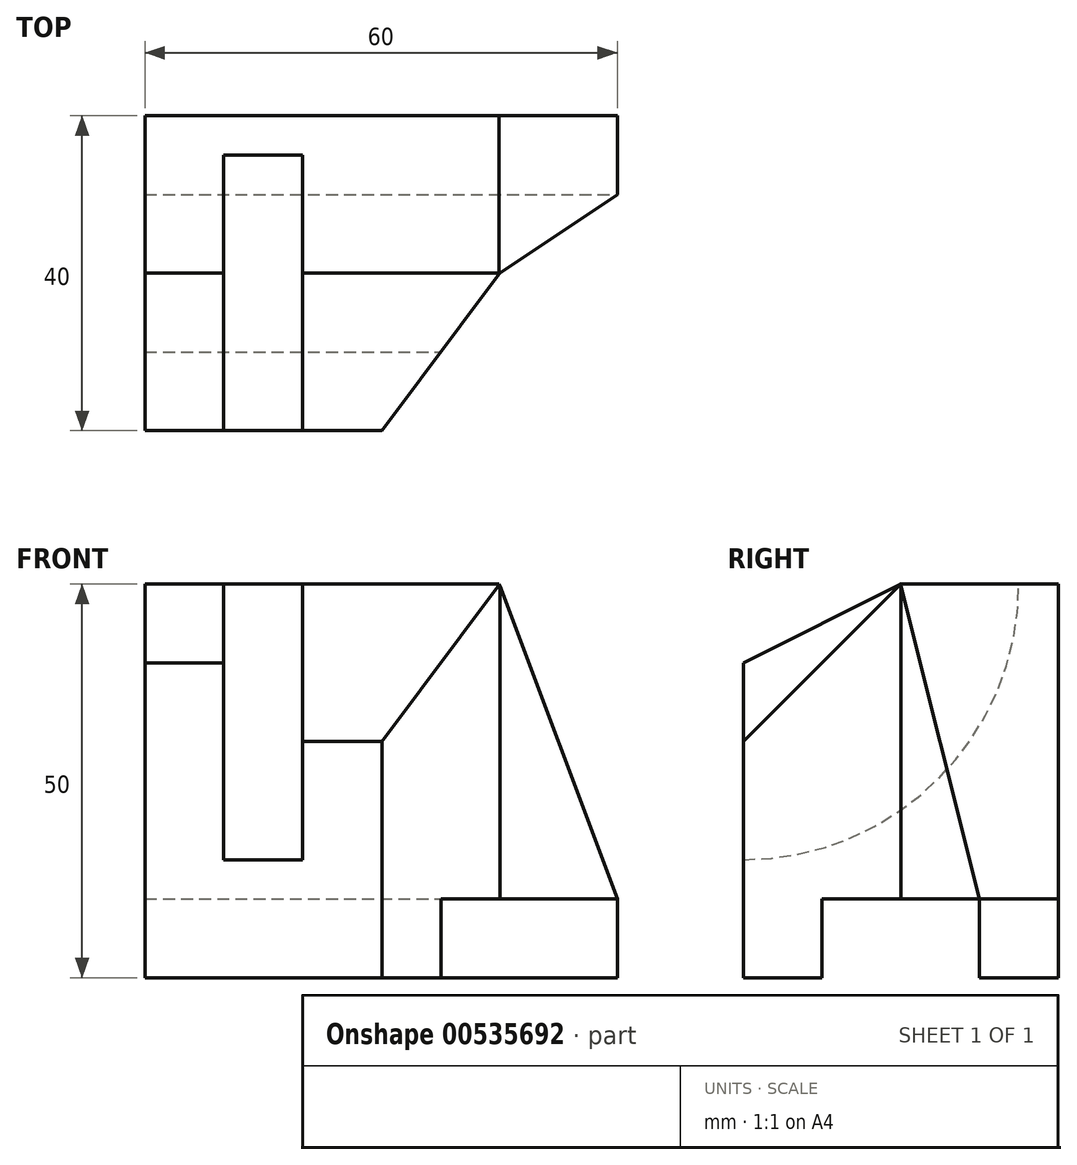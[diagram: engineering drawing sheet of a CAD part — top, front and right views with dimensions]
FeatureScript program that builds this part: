
annotation { "Feature Type Name" : "Feature", "Feature Type Description" : "" }
export const myFeature = defineFeature(function(context is Context, id is Id, definition is map)
    precondition{}
    {
        {
            var Q0;
            Q0=qCreatedBy(makeId("Top.planeOp"),FACE);
            var sketch = newSketch(context, id + "F0", { "sketchPlane" : qUnion([Q0])});
            skLineSegment(sketch, "E0.bottom", {"start": v(0, 0) * mm, "end": v(60, 0) * mm});
            skLineSegment(sketch, "E0.top", {"start": v(0, 40) * mm, "end": v(60, 40) * mm});
            skLineSegment(sketch, "E0.left", {"start": v(0, 0) * mm, "end": v(0, 40) * mm});
            skLineSegment(sketch, "E0.right", {"start": v(60, 0) * mm, "end": v(60, 40) * mm});
            skSolve(sketch);
        }
        {
            var Q0;
            Q0 = qSketchRegion(id + "F0", true);
            extrude(context, id + "F1", {"entities" : qUnion([Q0]), "depth" : 50 * mm, "offsetDistance" : 25 * mm});
        }
        {
            var Q0;
            Q0=makeQuery(id+"F1.opExtrude","SWEPT_FACE",FACE,{"disambiguationData":[OSD([sQuery(id+"F0.wireOp",EDGE,"E0.right")])]});
            var sketch = newSketch(context, id + "F2", { "sketchPlane" : qUnion([Q0])});
            skLineSegment(sketch, "E1", {"start": v(0, 0) * mm, "end": v(10, 0) * mm});
            skLineSegment(sketch, "E2.bottom", {"start": v(10, 0) * mm, "end": v(30, 0) * mm});
            skLineSegment(sketch, "E2.top", {"start": v(10, 10) * mm, "end": v(30, 10) * mm});
            skLineSegment(sketch, "E2.left", {"start": v(10, 0) * mm, "end": v(10, 10) * mm});
            skLineSegment(sketch, "E2.right", {"start": v(30, 0) * mm, "end": v(30, 10) * mm});
            skSolve(sketch);
        }
        {
            var Q0;
            Q0 = qSketchRegion(id + "F2", true);
            extrude(context, id + "F3", {"entities" : qUnion([Q0]), "operationType" : NewBodyOperationType.REMOVE, "endBound" : BoundingType.UP_TO_NEXT, "oppositeDirection" : true, "depth" : 25 * mm, "offsetDistance" : 25 * mm});
        }
        {
            var Q0;
            Q0=qCreatedBy(makeId("Right.planeOp"),FACE);
            cPlane(context, id + "F4", {"entities" : qUnion([Q0]), "cplaneType" : CPlaneType.OFFSET, "offset" : 10 * mm, "width" : 150 * mm, "height" : 150 * mm});
        }
        {
            var Q0;
            Q0=qCreatedBy(id+"F4.planeOp",FACE);
            cPlane(context, id + "F5", {"entities" : qUnion([Q0]), "cplaneType" : CPlaneType.OFFSET, "offset" : 10 * mm, "width" : 150 * mm, "height" : 150 * mm});
        }
        {
            var Q0;
            Q0=makeQuery(id+"F1.opExtrude","SWEPT_FACE",FACE,{"disambiguationData":[OSD([sQuery(id+"F0.wireOp",EDGE,"E0.left")])]});
            var sketch = newSketch(context, id + "F6", { "sketchPlane" : qUnion([Q0])});
            skLineSegment(sketch, "E3", {"start": v(0, 50) * mm, "end": v(0, 40) * mm});
            skLineSegment(sketch, "E4", {"start": v(0, 50) * mm, "end": v(-20, 50) * mm});
            skLineSegment(sketch, "E5", {"start": v(-20, 50) * mm, "end": v(0, 40) * mm});
            skSolve(sketch);
        }
        {
            var Q0;
            Q0 = qSketchRegion(id + "F6", true);
            var Q1;
            Q1=qCreatedBy(id+"F4.planeOp",FACE);
            extrude(context, id + "F7", {"entities" : qUnion([Q0]), "operationType" : NewBodyOperationType.REMOVE, "endBound" : BoundingType.UP_TO_SURFACE, "oppositeDirection" : true, "depth" : 25 * mm, "endBoundEntityFace" : qUnion([Q1]), "offsetDistance" : 25 * mm});
        }
        {
            var Q0;
            Q0=qCreatedBy(makeId("Right.planeOp"),FACE);
            cPlane(context, id + "F8", {"entities" : qUnion([Q0]), "cplaneType" : CPlaneType.OFFSET, "offset" : 45 * mm, "width" : 150 * mm, "height" : 150 * mm});
        }
        {
            var Q0;
            Q0=qCreatedBy(id+"F5.planeOp",FACE);
            var sketch = newSketch(context, id + "F9", { "sketchPlane" : qUnion([Q0])});
            skLineSegment(sketch, "E6", {"start": v(0, 50) * mm, "end": v(0, 30) * mm});
            skLineSegment(sketch, "E7", {"start": v(0, 50) * mm, "end": v(20, 50) * mm});
            skLineSegment(sketch, "E8", {"start": v(20, 50) * mm, "end": v(0, 30) * mm});
            skSolve(sketch);
        }
        {
            var Q0;
            Q0 = qSketchRegion(id + "F9", true);
            var Q1;
            Q1=qCreatedBy(id+"F8.planeOp",FACE);
            extrude(context, id + "F10", {"entities" : qUnion([Q0]), "operationType" : NewBodyOperationType.REMOVE, "endBound" : BoundingType.UP_TO_SURFACE, "depth" : 25 * mm, "endBoundEntityFace" : qUnion([Q1]), "offsetDistance" : 25 * mm});
        }
        {
            var Q0;
            Q0=qCreatedBy(id+"F4.planeOp",FACE);
            var sketch = newSketch(context, id + "F11", { "sketchPlane" : qUnion([Q0])});
            skCircle(sketch, "E9", {"center": v(0, 50) * mm, "radius": 35 * mm});
            skSolve(sketch);
        }
        {
            var Q0;
            Q0 = qSketchRegion(id + "F11", true);
            var Q1;
            Q1=qCreatedBy(id+"F5.planeOp",FACE);
            extrude(context, id + "F12", {"entities" : qUnion([Q0]), "operationType" : NewBodyOperationType.REMOVE, "endBound" : BoundingType.UP_TO_SURFACE, "depth" : 25 * mm, "endBoundEntityFace" : qUnion([Q1]), "offsetDistance" : 25 * mm});
        }
        {
            var Q0;
            Q0=qCreatedBy(makeId("Top.planeOp"),FACE);
            cPlane(context, id + "F13", {"entities" : qUnion([Q0]), "cplaneType" : CPlaneType.OFFSET, "offset" : 50 * mm, "width" : 150 * mm, "height" : 150 * mm});
        }
        {
            var Q0;
            Q0=qCreatedBy(id+"F13.planeOp",FACE);
            var sketch = newSketch(context, id + "F14", { "sketchPlane" : qUnion([Q0])});
            skLineSegment(sketch, "E10", {"start": v(45.1, 0) * mm, "end": v(45.1, 20) * mm});
            skLineSegment(sketch, "E11", {"start": v(45.1, 0) * mm, "end": v(30.1, 0) * mm});
            skLineSegment(sketch, "E12", {"start": v(45.1, 20) * mm, "end": v(30.1, 0) * mm});
            skSolve(sketch);
        }
        {
            var Q0;
            Q0 = qSketchRegion(id + "F14", true);
            extrude(context, id + "F15", {"entities" : qUnion([Q0]), "operationType" : NewBodyOperationType.REMOVE, "oppositeDirection" : true, "depth" : 50 * mm, "offsetDistance" : 25 * mm});
        }
        {
            var Q0;
            Q0=makeQuery(id+"F1.opExtrude","CAP_FACE",FACE,{"disambiguationData":[OSD([sQuery(id+"F0.wireOp",EDGE,"E0.bottom"),sQuery(id+"F0.wireOp",EDGE,"E0.top"),sQuery(id+"F0.wireOp",EDGE,"E0.left"),sQuery(id+"F0.wireOp",EDGE,"E0.right")])],"isStart":false});
            var sketch = newSketch(context, id + "F16", { "sketchPlane" : qUnion([Q0])});
            skLineSegment(sketch, "E13", {"start": v(60, 40) * mm, "end": v(60, 30) * mm});
            skLineSegment(sketch, "E14", {"start": v(60, 30) * mm, "end": v(45.1, 20) * mm});
            skLineSegment(sketch, "E15", {"start": v(45.1, 20) * mm, "end": v(45.1, 0) * mm});
            skLineSegment(sketch, "E16", {"start": v(45.1, 0) * mm, "end": v(60, 0) * mm});
            skLineSegment(sketch, "E17", {"start": v(60, 0) * mm, "end": v(60, 30) * mm});
            skSolve(sketch);
        }
        {
            var Q0;
            Q0 = qSketchRegion(id + "F16", true);
            extrude(context, id + "F17", {"entities" : qUnion([Q0]), "operationType" : NewBodyOperationType.REMOVE, "endBound" : BoundingType.UP_TO_NEXT, "oppositeDirection" : true, "depth" : 25 * mm, "offsetDistance" : 25 * mm});
        }
        {
            var Q0;
            Q0=makeQuery(id+"F1.opExtrude","SWEPT_FACE",FACE,{"disambiguationData":[OSD([sQuery(id+"F0.wireOp",EDGE,"E0.top")])]});
            var sketch = newSketch(context, id + "F18", { "sketchPlane" : qUnion([Q0])});
            skLineSegment(sketch, "E18", {"start": v(-60, 50) * mm, "end": v(-45, 50) * mm});
            skLineSegment(sketch, "E19", {"start": v(-60, 0) * mm, "end": v(-60, 10) * mm});
            skLineSegment(sketch, "E20", {"start": v(-45, 50) * mm, "end": v(-60, 10) * mm});
            skLineSegment(sketch, "E21", {"start": v(-60, 10) * mm, "end": v(-60, 50) * mm});
            skSolve(sketch);
        }
        {
            var Q0;
            Q0 = qSketchRegion(id + "F18", true);
            extrude(context, id + "F19", {"entities" : qUnion([Q0]), "operationType" : NewBodyOperationType.REMOVE, "endBound" : BoundingType.UP_TO_NEXT, "oppositeDirection" : true, "depth" : 25 * mm, "offsetDistance" : 25 * mm});
        }
    });
